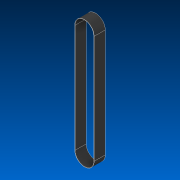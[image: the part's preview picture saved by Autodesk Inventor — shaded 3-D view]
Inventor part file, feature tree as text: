
AUTODESK INVENTOR PART (.ipt)
format: ipt  version: 2022 (Build 260153000, 153)  size: 93,184 bytes
history: native  units: in
note: dims shown in document units (in); Inventor stores cm internally (conversion verified against a paired STEP export)
features: extrude x1, sketch x1
ambient origin geometry x8: Origin, YZ Plane, XZ Plane, XY Plane, X Axis, Y Axis, Z Axis, Center Point
bodies: Solid1 (feature_tree)
feature tree (2):
  extrude  "Extrusion1"  Depth=1.75in
  sketch  "Sketch1"  dims[d0=19.5in d1=1.75in d2=0.0625in d3=2.0in d4=0.0in]
